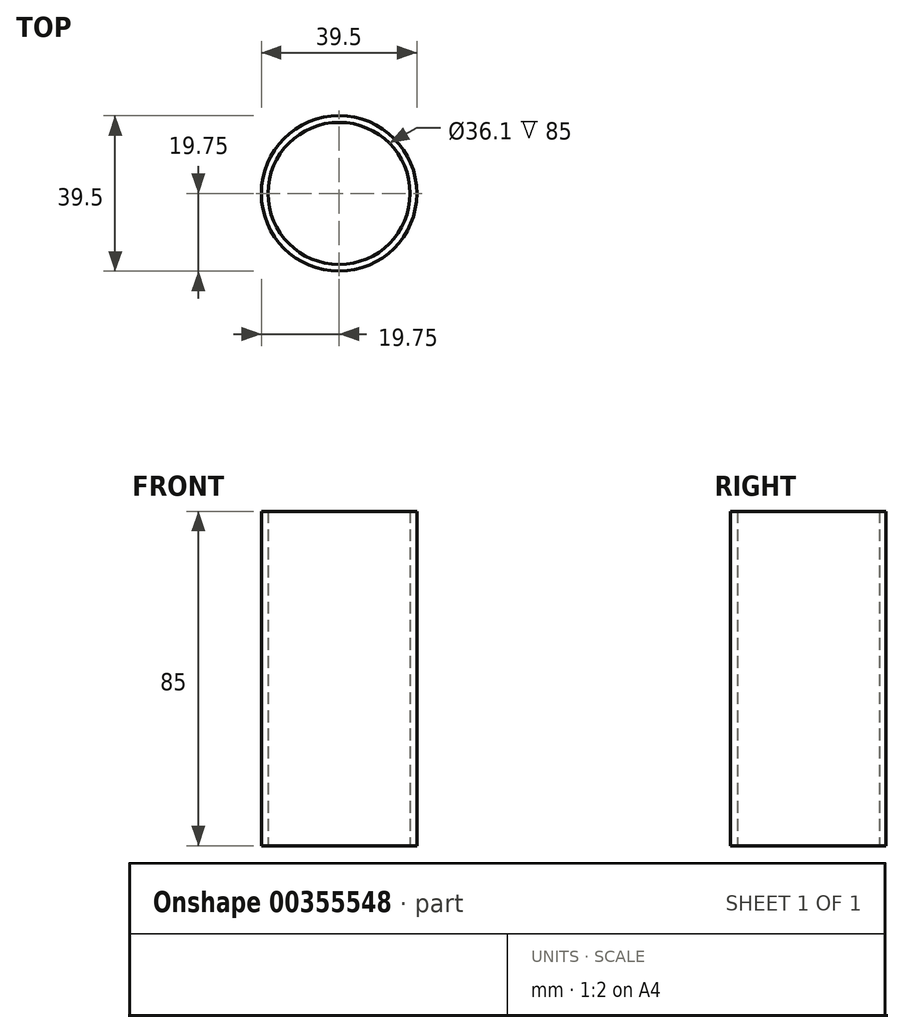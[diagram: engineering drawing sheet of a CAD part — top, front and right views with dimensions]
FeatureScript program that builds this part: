
annotation { "Feature Type Name" : "Feature", "Feature Type Description" : "" }
export const myFeature = defineFeature(function(context is Context, id is Id, definition is map)
    precondition{}
    {
        {
            var Q0;
            Q0=qCreatedBy(makeId("Top.planeOp"),FACE);
            var sketch = newSketch(context, id + "F0", { "sketchPlane" : qUnion([Q0])});
            skCircle(sketch, "E0", {"center": v(0, 0) * mm, "radius": 19.75 * mm});
            skCircle(sketch, "E1.0", {"center": v(0, 0) * mm, "radius": 18.05 * mm});
            skSolve(sketch);
        }
        {
            var Q0;
            Q0 = qSketchRegion(id + "F0", true);
            extrude(context, id + "F1", {"entities" : qUnion([Q0]), "depth" : 85 * mm});
        }
    });
